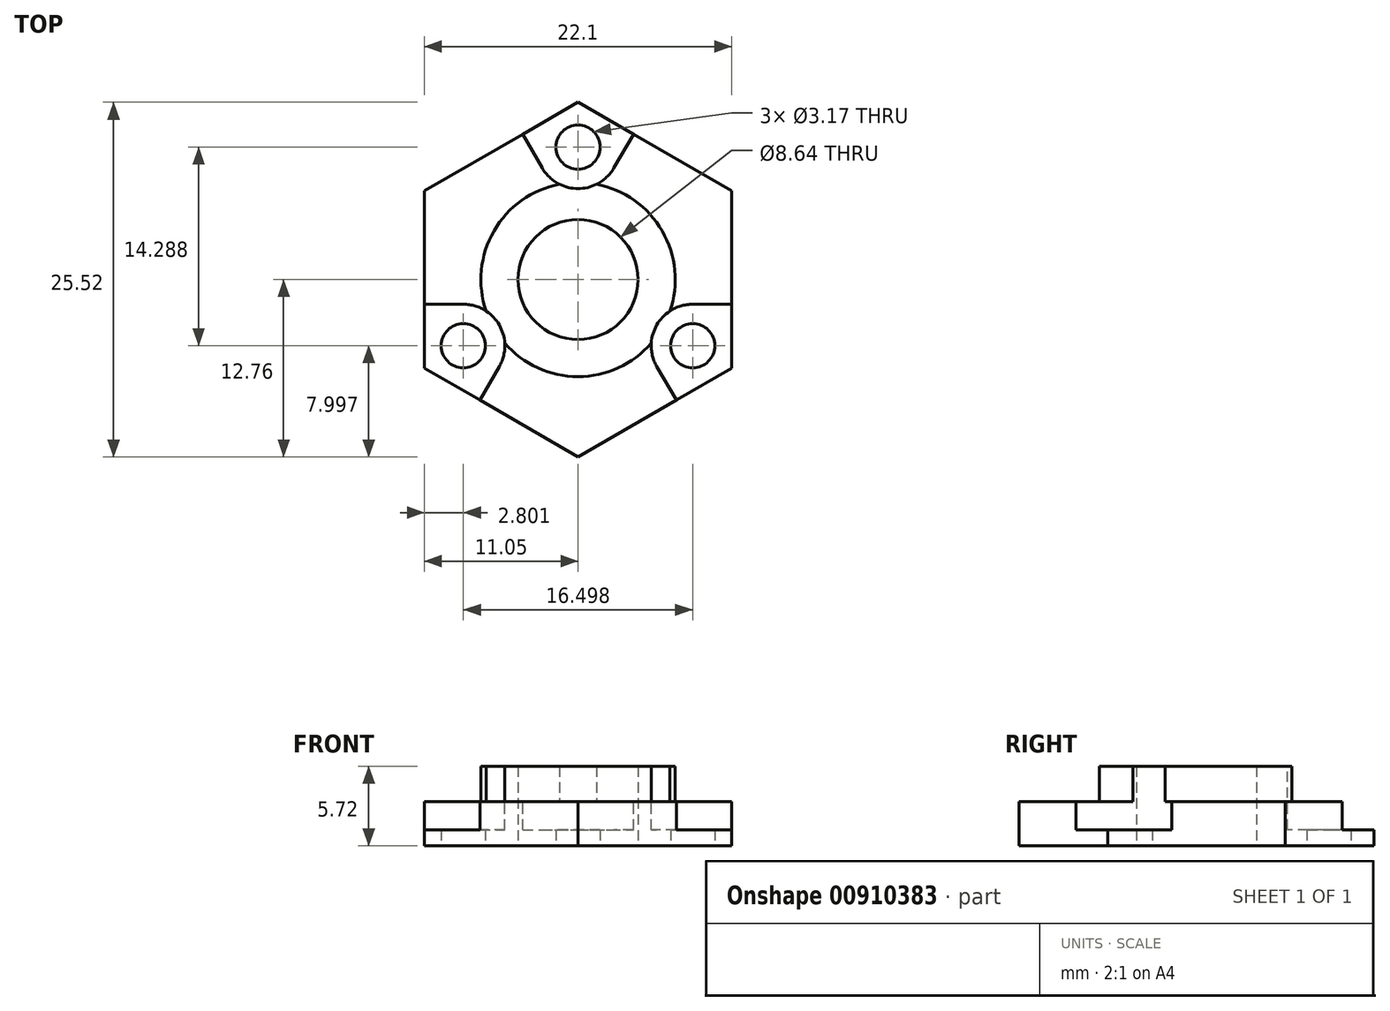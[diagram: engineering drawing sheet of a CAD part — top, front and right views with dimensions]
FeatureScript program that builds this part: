
annotation { "Feature Type Name" : "Feature", "Feature Type Description" : "" }
export const myFeature = defineFeature(function(context is Context, id is Id, definition is map)
    precondition{}
    {
        {
            var Q0;
            Q0=qCreatedBy(makeId("Top.planeOp"),FACE);
            var sketch = newSketch(context, id + "F0", { "sketchPlane" : qUnion([Q0])});
            skCircle(sketch, "E0.cCircle", {"center": v(0, 0) * mm, "radius": 11.05 * mm, "construction": true});
            skLineSegment(sketch, "E0.0", {"start": v(11.05, 6.38) * mm, "end": v(11.05, -6.38) * mm});
            skLineSegment(sketch, "E0.1", {"start": v(11.05, -6.38) * mm, "end": v(0, -12.76) * mm});
            skLineSegment(sketch, "E0.2", {"start": v(0, -12.76) * mm, "end": v(-11.05, -6.38) * mm});
            skLineSegment(sketch, "E0.3", {"start": v(-11.05, -6.38) * mm, "end": v(-11.05, 6.38) * mm});
            skLineSegment(sketch, "E0.4", {"start": v(-11.05, 6.38) * mm, "end": v(0, 12.76) * mm});
            skLineSegment(sketch, "E0.5", {"start": v(0, 12.76) * mm, "end": v(11.05, 6.38) * mm});
            skPoint(sketch, "E0.0.midPoint", {"position": v(11.05, 0) * mm});
            skCircle(sketch, "E1", {"center": v(-8.25, -4.76) * mm, "radius": 1.59 * mm});
            skCircle(sketch, "E2", {"center": v(8.25, -4.76) * mm, "radius": 1.59 * mm});
            skCircle(sketch, "E3", {"center": v(0, 9.53) * mm, "radius": 1.59 * mm});
            skLineSegment(sketch, "E4", {"start": v(-8.25, -4.76) * mm, "end": v(0, 9.52) * mm, "construction": true});
            skLineSegment(sketch, "E5", {"start": v(8.25, -4.76) * mm, "end": v(-8.25, -4.76) * mm, "construction": true});
            skLineSegment(sketch, "E6", {"start": v(0, 9.53) * mm, "end": v(8.25, -4.76) * mm, "construction": true});
            skLineSegment(sketch, "E7", {"start": v(0, 9.53) * mm, "end": v(0, 0) * mm, "construction": true});
            skLineSegment(sketch, "E8", {"start": v(8.25, -4.76) * mm, "end": v(0, 0) * mm, "construction": true});
            skCircle(sketch, "E9", {"center": v(0, 0) * mm, "radius": 4.32 * mm});
            skSolve(sketch);
        }
        {
            var Q0;
            Q0 = qSketchRegion(id + "F0", true);
            extrude(context, id + "F1", {"entities" : qUnion([Q0]), "depth" : 3.17 * mm, "offsetDistance" : 25.4 * mm});
        }
        {
            var Q0;
            Q0=makeQuery(id+"F1.opExtrude","CAP_FACE",FACE,{"disambiguationData":[OSD([sQuery(id+"F0.wireOp",EDGE,"E0.0"),sQuery(id+"F0.wireOp",EDGE,"E0.1"),sQuery(id+"F0.wireOp",EDGE,"E0.2"),sQuery(id+"F0.wireOp",EDGE,"E0.3"),sQuery(id+"F0.wireOp",EDGE,"E0.4"),sQuery(id+"F0.wireOp",EDGE,"E0.5"),sQuery(id+"F0.wireOp",EDGE,"E1"),sQuery(id+"F0.wireOp",EDGE,"E2"),sQuery(id+"F0.wireOp",EDGE,"E3")])],"isStart":false});
            var sketch = newSketch(context, id + "F2", { "sketchPlane" : qUnion([Q0])});
            skCircle(sketch, "E10", {"center": v(0, 9.53) * mm, "radius": 2.98 * mm, "construction": true});
            skLineSegment(sketch, "E11", {"start": v(-3.98, 10.46) * mm, "end": v(0, 12.76) * mm});
            skLineSegment(sketch, "E12", {"start": v(0, 12.76) * mm, "end": v(3.98, 10.46) * mm});
            skLineSegment(sketch, "E13", {"start": v(3.98, 10.46) * mm, "end": v(2.58, 8.03) * mm});
            skLineSegment(sketch, "E14", {"start": v(-3.98, 10.46) * mm, "end": v(-2.58, 8.03) * mm});
            skArc(sketch, "E15", {"start": v(-2.58, 8.03) * mm, "mid": v(0, 6.54) * mm, "end": v(2.58, 8.03) * mm});
            skLineSegment(sketch, "E16.1.0", {"start": v(-11.05, -1.78) * mm, "end": v(-8.25, -1.78) * mm});
            skLineSegment(sketch, "E16.1.1", {"start": v(-11.05, -6.38) * mm, "end": v(-11.05, -1.78) * mm});
            skLineSegment(sketch, "E16.1.2", {"start": v(-7.06, -8.68) * mm, "end": v(-11.05, -6.38) * mm});
            skLineSegment(sketch, "E16.1.3", {"start": v(-7.06, -8.68) * mm, "end": v(-5.66, -6.25) * mm});
            skArc(sketch, "E16.1.4", {"start": v(-5.66, -6.25) * mm, "mid": v(-5.66, -3.27) * mm, "end": v(-8.25, -1.78) * mm});
            skLineSegment(sketch, "E16.2.0", {"start": v(7.06, -8.68) * mm, "end": v(5.66, -6.25) * mm});
            skLineSegment(sketch, "E16.2.1", {"start": v(11.05, -6.38) * mm, "end": v(7.06, -8.68) * mm});
            skLineSegment(sketch, "E16.2.2", {"start": v(11.05, -1.78) * mm, "end": v(11.05, -6.38) * mm});
            skLineSegment(sketch, "E16.2.3", {"start": v(11.05, -1.78) * mm, "end": v(8.25, -1.78) * mm});
            skArc(sketch, "E16.2.4", {"start": v(8.25, -1.78) * mm, "mid": v(5.66, -3.27) * mm, "end": v(5.66, -6.25) * mm});
            skPoint(sketch, "E16.center", {"position": v(0, 0) * mm});
            skSolve(sketch);
        }
        {
            var Q0;
            Q0 = qSketchRegion(id + "F2", true);
            extrude(context, id + "F3", {"entities" : qUnion([Q0]), "operationType" : NewBodyOperationType.REMOVE, "oppositeDirection" : true, "depth" : 2.03 * mm, "offsetDistance" : 25.4 * mm});
        }
        {
            var Q0;
            Q0=makeQuery(id+"F1.opExtrude","CAP_FACE",FACE,{"disambiguationData":[OSD([sQuery(id+"F0.wireOp",EDGE,"E0.0"),sQuery(id+"F0.wireOp",EDGE,"E0.1"),sQuery(id+"F0.wireOp",EDGE,"E0.2"),sQuery(id+"F0.wireOp",EDGE,"E0.3"),sQuery(id+"F0.wireOp",EDGE,"E0.4"),sQuery(id+"F0.wireOp",EDGE,"E0.5"),sQuery(id+"F0.wireOp",EDGE,"E1"),sQuery(id+"F0.wireOp",EDGE,"E2"),sQuery(id+"F0.wireOp",EDGE,"E3"),sQuery(id+"F0.wireOp",EDGE,"E9")])],"isStart":false});
            var sketch = newSketch(context, id + "F4", { "sketchPlane" : qUnion([Q0])});
            skCircle(sketch, "E17", {"center": v(0, 0) * mm, "radius": 7.62 * mm, "construction": true});
            skCircle(sketch, "E18", {"center": v(0, 0) * mm, "radius": 9.02 * mm, "construction": true});
            skSolve(sketch);
        }
        {
            var Q0;
            Q0=makeQuery(id+"F4.imprint","IMPRINT",FACE,{"disambiguationData":[TD([[makeQuery(id+"F4.imprint","IMPRINT",EDGE,{"derivedFrom":makeQuery(id+"F1.opExtrude","CAP_EDGE",EDGE,{"disambiguationData":[OSD([sQuery(id+"F0.wireOp",EDGE,"E9")])],"isStart":false})}),-1.0]])]});
            var sketch = newSketch(context, id + "F5", { "sketchPlane" : qUnion([Q0])});
            skArc(sketch, "E19", {"start": v(-5.27, -4.58) * mm, "mid": v(0, -6.99) * mm, "end": v(5.27, -4.58) * mm});
            skCircle(sketch, "E20.0", {"center": v(0, 0) * mm, "radius": 4.32 * mm});
            skArc(sketch, "E21.0", {"start": v(-1.34, 6.86) * mm, "mid": v(0, 6.54) * mm, "end": v(1.34, 6.86) * mm});
            skArc(sketch, "E21.1", {"start": v(6.6, -2.27) * mm, "mid": v(5.66, -3.27) * mm, "end": v(5.27, -4.58) * mm});
            skArc(sketch, "E21.2", {"start": v(-5.27, -4.58) * mm, "mid": v(-5.66, -3.27) * mm, "end": v(-6.6, -2.27) * mm});
            skPoint(sketch, "E22.orphan", {"position": v(-8.25, -1.78) * mm});
            skPoint(sketch, "E23.orphan", {"position": v(-5.66, -6.25) * mm});
            skPoint(sketch, "E24.orphan", {"position": v(-2.58, 8.03) * mm});
            skArc(sketch, "E25.trimOffspring", {"start": v(-1.34, 6.86) * mm, "mid": v(-6.05, 3.5) * mm, "end": v(-6.6, -2.27) * mm});
            skPoint(sketch, "E26.orphan", {"position": v(2.58, 8.03) * mm});
            skPoint(sketch, "E27.orphan", {"position": v(5.66, -6.25) * mm});
            skArc(sketch, "E28.trimOffspring", {"start": v(6.6, -2.27) * mm, "mid": v(6.05, 3.5) * mm, "end": v(1.34, 6.86) * mm});
            skPoint(sketch, "E29.orphan", {"position": v(8.25, -1.78) * mm});
            skSolve(sketch);
        }
        {
            var Q0;
            Q0 = qSketchRegion(id + "F5", true);
            extrude(context, id + "F6", {"entities" : qUnion([Q0]), "operationType" : NewBodyOperationType.ADD, "depth" : 2.54 * mm, "offsetDistance" : 25.4 * mm});
        }
    });
